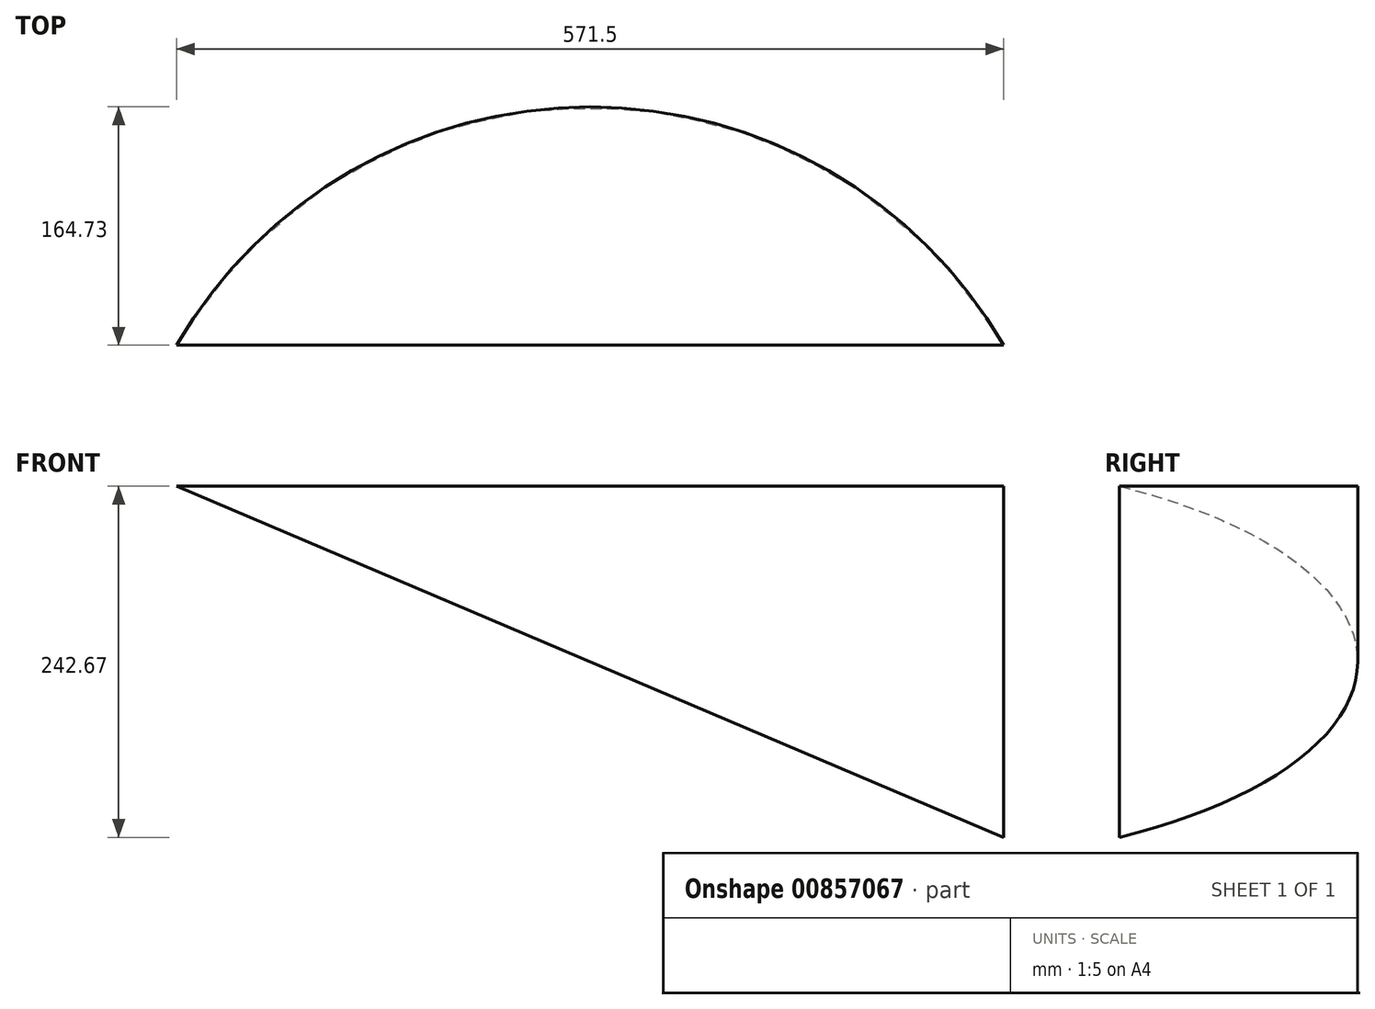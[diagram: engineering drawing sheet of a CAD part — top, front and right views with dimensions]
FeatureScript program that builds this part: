
annotation { "Feature Type Name" : "Feature", "Feature Type Description" : "" }
export const myFeature = defineFeature(function(context is Context, id is Id, definition is map)
    precondition{}
    {
        {
            var Q0;
            Q0=qCreatedBy(makeId("Top.planeOp"),FACE);
            var sketch = newSketch(context, id + "F0", { "sketchPlane" : qUnion([Q0])});
            skLineSegment(sketch, "E0", {"start": v(-285.75, 0) * mm, "end": v(285.75, 0) * mm});
            skArc(sketch, "E1", {"start": v(285.75, 0) * mm, "mid": v(0, 164.73) * mm, "end": v(-285.75, 0) * mm});
            skSolve(sketch);
        }
        {
            var Q0;
            Q0=makeQuery(id+"F0.imprint","IMPRINT",FACE,{"disambiguationData":[TD([[makeQuery(id+"F0.imprint","IMPRINT",EDGE,{"derivedFrom":sQuery(id+"F0.wireOp",EDGE,"E0")}),1.0]])]});
            extrude(context, id + "F1", {"entities" : qUnion([Q0]), "depth" : 242.67 * mm, "offsetDistance" : 25.4 * mm});
        }
        {
            var Q0;
            Q0=makeQuery(id+"F1.opExtrude","SWEPT_FACE",FACE,{"disambiguationData":[OSD([sQuery(id+"F0.wireOp",EDGE,"E0")])]});
            var sketch = newSketch(context, id + "F2", { "sketchPlane" : qUnion([Q0])});
            skLineSegment(sketch, "E2", {"start": v(-285.75, 242.67) * mm, "end": v(285.75, 0) * mm});
            skLineSegment(sketch, "E3", {"start": v(285.75, 0) * mm, "end": v(-285.75, 0) * mm});
            skLineSegment(sketch, "E4", {"start": v(-285.75, 0) * mm, "end": v(-285.75, 242.67) * mm});
            skSolve(sketch);
        }
        {
            var Q0;
            Q0=makeQuery(id+"F2.imprint","IMPRINT",FACE,{"disambiguationData":[TD([[makeQuery(id+"F2.imprint","IMPRINT",EDGE,{"derivedFrom":sQuery(id+"F2.wireOp",EDGE,"E2")}),-1.0]])]});
            extrude(context, id + "F3", {"entities" : qUnion([Q0]), "operationType" : NewBodyOperationType.REMOVE, "oppositeDirection" : true, "depth" : 508 * mm, "offsetDistance" : 25.4 * mm});
        }
    });
